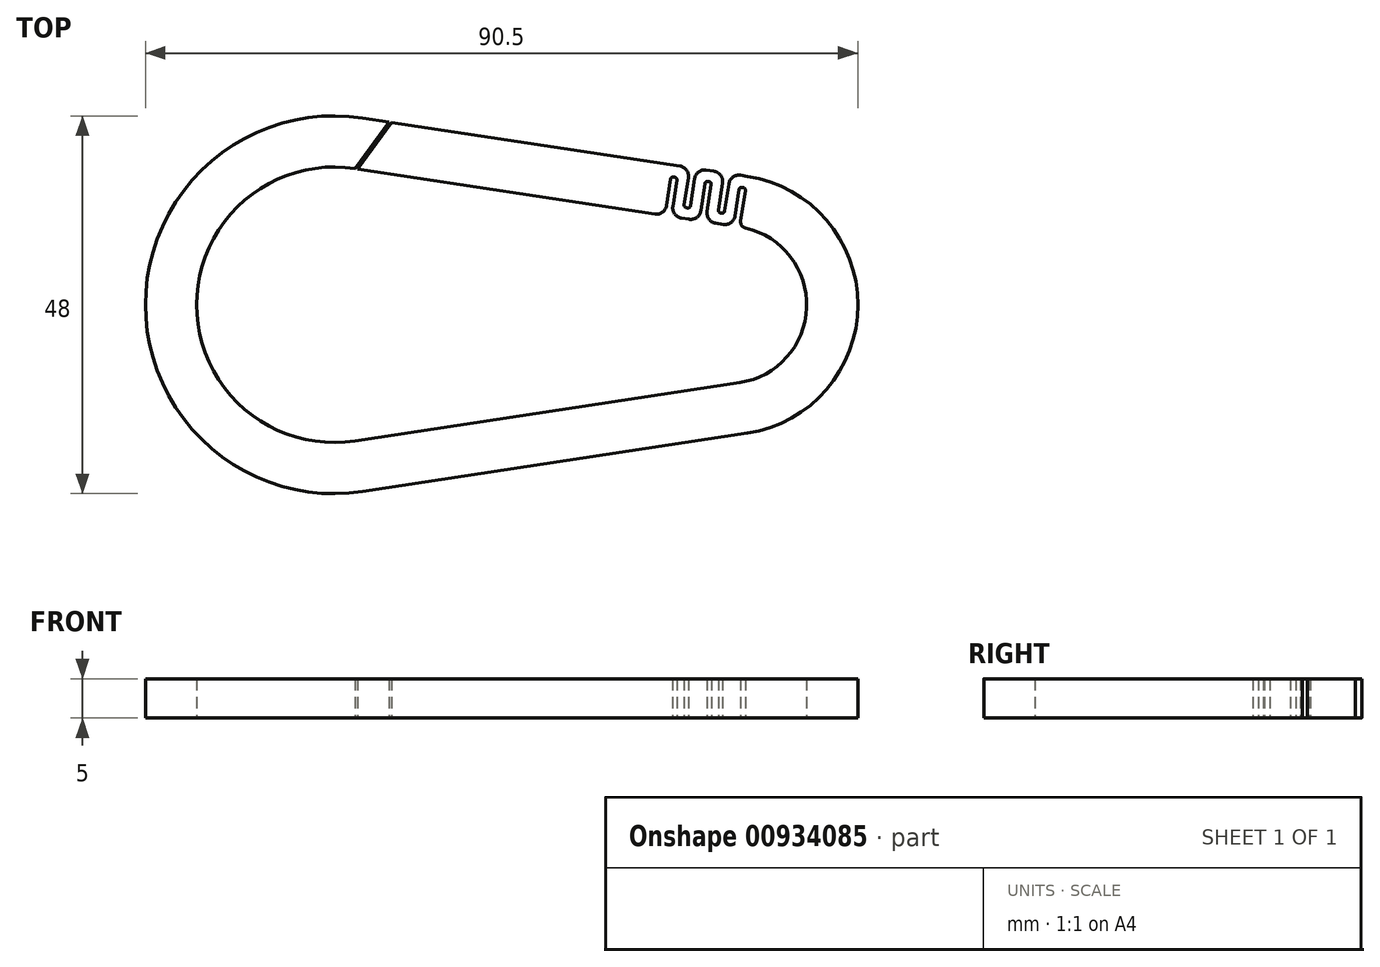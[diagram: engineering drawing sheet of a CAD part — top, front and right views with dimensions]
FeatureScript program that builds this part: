
annotation { "Feature Type Name" : "Feature", "Feature Type Description" : "" }
export const myFeature = defineFeature(function(context is Context, id is Id, definition is map)
    precondition{}
    {
        {
            var Q0;
            Q0=qCreatedBy(makeId("Top.planeOp"),FACE);
            var sketch = newSketch(context, id + "F0", { "sketchPlane" : qUnion([Q0])});
            skArc(sketch, "E0", {"start": v(1.5, -9.89) * mm, "mid": v(10, -0.37) * mm, "end": v(2.23, 9.75) * mm});
            skArc(sketch, "E1", {"start": v(-47.38, 17.3) * mm, "mid": v(-67.5, 0) * mm, "end": v(-47.37, -17.3) * mm});
            skLineSegment(sketch, "E2", {"start": v(-47.38, -17.3) * mm, "end": v(1.5, -9.89) * mm});
            skLineSegment(sketch, "E3", {"start": v(-47.04, 17.25) * mm, "end": v(-9.28, 11.52) * mm});
            skArc(sketch, "E4.0", {"start": v(-46.4, 23.73) * mm, "mid": v(-74, 0) * mm, "end": v(-46.4, -23.73) * mm});
            skLineSegment(sketch, "E4.1", {"start": v(-46.4, 23.73) * mm, "end": v(-43.06, 23.22) * mm});
            skArc(sketch, "E4.2", {"start": v(2.48, -16.31) * mm, "mid": v(16.5, 0) * mm, "end": v(2.47, 16.31) * mm});
            skLineSegment(sketch, "E4.3", {"start": v(-46.4, -23.73) * mm, "end": v(2.48, -16.31) * mm});
            skLineSegment(sketch, "E5", {"start": v(-47.38, 17.3) * mm, "end": v(-43.06, 23.22) * mm});
            skLineSegment(sketch, "E6", {"start": v(-42.73, 23.17) * mm, "end": v(-47.04, 17.25) * mm});
            skLineSegment(sketch, "E7.trimOffspring", {"start": v(-42.73, 23.17) * mm, "end": v(-6.13, 17.62) * mm});
            skLineSegment(sketch, "E8", {"start": v(1.62, 10.65) * mm, "end": v(2.2, 14.53) * mm});
            skLineSegment(sketch, "E9", {"start": v(1.95, 14.88) * mm, "end": v(1.76, 14.9) * mm});
            skLineSegment(sketch, "E10", {"start": v(1.41, 14.65) * mm, "end": v(0.9, 11.3) * mm});
            skLineSegment(sketch, "E11", {"start": v(0.1, 15.36) * mm, "end": v(-0.42, 11.9) * mm});
            skLineSegment(sketch, "E12", {"start": v(-0.76, 11.65) * mm, "end": v(-0.96, 11.68) * mm});
            skLineSegment(sketch, "E13", {"start": v(-1.21, 12.02) * mm, "end": v(-0.69, 15.48) * mm});
            skLineSegment(sketch, "E14", {"start": v(-2.66, 11.83) * mm, "end": v(-2.13, 15.3) * mm});
            skLineSegment(sketch, "E15", {"start": v(-2.38, 15.63) * mm, "end": v(-2.58, 15.66) * mm});
            skLineSegment(sketch, "E16", {"start": v(-2.92, 15.41) * mm, "end": v(-3.45, 11.95) * mm});
            skLineSegment(sketch, "E17.trimOffspring", {"start": v(1.59, 16.45) * mm, "end": v(2.47, 16.31) * mm});
            skLineSegment(sketch, "E18.trimOffspring", {"start": v(-1.56, 10.35) * mm, "end": v(-0.58, 10.2) * mm});
            skPoint(sketch, "E19.visualSharp", {"position": v(-1.26, 11.72) * mm});
            skArc(sketch, "E19.filletArc", {"start": v(-1.21, 12.02) * mm, "mid": v(-1.16, 11.8) * mm, "end": v(-0.96, 11.68) * mm});
            skPoint(sketch, "E20.visualSharp", {"position": v(-0.47, 11.6) * mm});
            skArc(sketch, "E20.filletArc", {"start": v(-0.76, 11.65) * mm, "mid": v(-0.54, 11.7) * mm, "end": v(-0.42, 11.9) * mm});
            skPoint(sketch, "E21.visualSharp", {"position": v(1.46, 14.95) * mm});
            skArc(sketch, "E21.filletArc", {"start": v(1.76, 14.9) * mm, "mid": v(1.53, 14.85) * mm, "end": v(1.41, 14.65) * mm});
            skPoint(sketch, "E22.visualSharp", {"position": v(2.25, 14.83) * mm});
            skArc(sketch, "E22.filletArc", {"start": v(2.2, 14.53) * mm, "mid": v(2.15, 14.76) * mm, "end": v(1.95, 14.88) * mm});
            skPoint(sketch, "E23.visualSharp", {"position": v(-2.09, 15.59) * mm});
            skArc(sketch, "E23.filletArc", {"start": v(-2.13, 15.3) * mm, "mid": v(-2.19, 15.52) * mm, "end": v(-2.38, 15.63) * mm});
            skPoint(sketch, "E24.visualSharp", {"position": v(-2.88, 15.7) * mm});
            skArc(sketch, "E24.filletArc", {"start": v(-2.58, 15.66) * mm, "mid": v(-2.8, 15.6) * mm, "end": v(-2.92, 15.41) * mm});
            skPoint(sketch, "E25.visualSharp", {"position": v(-0.5, 16.76) * mm});
            skArc(sketch, "E25.filletArc", {"start": v(-0.69, 15.48) * mm, "mid": v(-0.92, 16.44) * mm, "end": v(-1.78, 16.96) * mm});
            skPoint(sketch, "E26.visualSharp", {"position": v(0.7, 10) * mm});
            skArc(sketch, "E26.filletArc", {"start": v(-0.58, 10.2) * mm, "mid": v(0.39, 10.44) * mm, "end": v(0.9, 11.3) * mm});
            skPoint(sketch, "E27.visualSharp", {"position": v(0.3, 16.64) * mm});
            skArc(sketch, "E27.filletArc", {"start": v(1.59, 16.45) * mm, "mid": v(0.62, 16.2) * mm, "end": v(0.1, 15.36) * mm});
            skPoint(sketch, "E28.visualSharp", {"position": v(-2.85, 10.55) * mm});
            skArc(sketch, "E28.filletArc", {"start": v(-2.66, 11.83) * mm, "mid": v(-2.42, 10.87) * mm, "end": v(-1.56, 10.35) * mm});
            skPoint(sketch, "E29.visualSharp", {"position": v(1.5, 9.89) * mm});
            skArc(sketch, "E29.filletArc", {"start": v(1.62, 10.65) * mm, "mid": v(1.75, 10.08) * mm, "end": v(2.23, 9.75) * mm});
            skPoint(sketch, "E30.visualSharp", {"position": v(-3.64, 10.67) * mm});
            skArc(sketch, "E30.filletArc", {"start": v(-4.93, 10.86) * mm, "mid": v(-3.96, 11.1) * mm, "end": v(-3.45, 11.95) * mm});
            skLineSegment(sketch, "E31", {"start": v(-4.25, 16.02) * mm, "end": v(-4.77, 12.56) * mm});
            skLineSegment(sketch, "E32", {"start": v(-5.11, 12.3) * mm, "end": v(-5.3, 12.34) * mm});
            skLineSegment(sketch, "E33", {"start": v(-5.56, 12.68) * mm, "end": v(-5.04, 16.14) * mm});
            skLineSegment(sketch, "E34.trimOffspring", {"start": v(-2.77, 17.1) * mm, "end": v(-1.78, 16.96) * mm});
            skLineSegment(sketch, "E35", {"start": v(-7, 12.5) * mm, "end": v(-6.5, 15.85) * mm});
            skLineSegment(sketch, "E36", {"start": v(-6.75, 16.2) * mm, "end": v(-6.94, 16.23) * mm});
            skLineSegment(sketch, "E37", {"start": v(-7.29, 15.97) * mm, "end": v(-7.8, 12.61) * mm});
            skLineSegment(sketch, "E38.trimOffspring", {"start": v(-5.92, 11.01) * mm, "end": v(-4.93, 10.86) * mm});
            skPoint(sketch, "E39.visualSharp", {"position": v(-4.82, 12.26) * mm});
            skArc(sketch, "E39.filletArc", {"start": v(-5.11, 12.3) * mm, "mid": v(-4.89, 12.36) * mm, "end": v(-4.77, 12.56) * mm});
            skPoint(sketch, "E40.visualSharp", {"position": v(-5.6, 12.38) * mm});
            skArc(sketch, "E40.filletArc", {"start": v(-5.56, 12.68) * mm, "mid": v(-5.5, 12.45) * mm, "end": v(-5.3, 12.34) * mm});
            skPoint(sketch, "E41.visualSharp", {"position": v(-6.45, 16.15) * mm});
            skArc(sketch, "E41.filletArc", {"start": v(-6.5, 15.85) * mm, "mid": v(-6.55, 16.08) * mm, "end": v(-6.75, 16.2) * mm});
            skPoint(sketch, "E42.visualSharp", {"position": v(-7.24, 16.27) * mm});
            skArc(sketch, "E42.filletArc", {"start": v(-6.94, 16.23) * mm, "mid": v(-7.17, 16.17) * mm, "end": v(-7.29, 15.97) * mm});
            skPoint(sketch, "E43.visualSharp", {"position": v(-4.84, 17.42) * mm});
            skArc(sketch, "E43.filletArc", {"start": v(-5.04, 16.14) * mm, "mid": v(-5.27, 17.1) * mm, "end": v(-6.13, 17.62) * mm});
            skPoint(sketch, "E44.visualSharp", {"position": v(-4.05, 17.3) * mm});
            skArc(sketch, "E44.filletArc", {"start": v(-2.77, 17.1) * mm, "mid": v(-3.73, 16.87) * mm, "end": v(-4.25, 16.02) * mm});
            skPoint(sketch, "E45.visualSharp", {"position": v(-7.2, 11.2) * mm});
            skArc(sketch, "E45.filletArc", {"start": v(-7, 12.5) * mm, "mid": v(-6.77, 11.53) * mm, "end": v(-5.92, 11.01) * mm});
            skPoint(sketch, "E46.visualSharp", {"position": v(-8, 11.33) * mm});
            skArc(sketch, "E46.filletArc", {"start": v(-9.28, 11.52) * mm, "mid": v(-8.31, 11.76) * mm, "end": v(-7.8, 12.61) * mm});
            skSolve(sketch);
        }
        {
            var Q0;
            Q0 = qSketchRegion(id + "F0", true);
            extrude(context, id + "F1", {"entities" : qUnion([Q0]), "depth" : 5 * mm, "offsetDistance" : 25 * mm});
        }
    });
